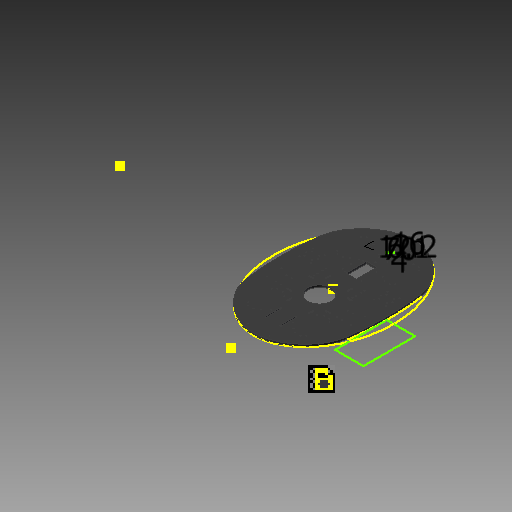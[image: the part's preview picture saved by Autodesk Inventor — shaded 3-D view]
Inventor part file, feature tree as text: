
AUTODESK INVENTOR PART (.ipt)
format: ipt  version: 2018 (Build 220112000, 112)  size: 756,224 bytes
history: native  units: in
note: dims shown in document units (in); Inventor stores cm internally (conversion verified against a paired STEP export)
features: reference x39, other x20, sketch x14, extrude x13, fillet x1, projected_geometry x1
ambient origin geometry x8: Origin, YZ Plane, XZ Plane, XY Plane, X Axis, Y Axis, Z Axis, Center Point
bodies: Body1 (feature_tree)
feature tree (88):
  extrude  "Extrusion2"  Depth=0.25in
  sketch  "Sketch2"  dims[d4=0.25in d5=0.0in d6=0.1969in]
  sketch  "Sketch3"  dims[d7=0.1969in d24=0.5in]
  extrude  "Extrusion13"  Depth=0.5in
  extrude  "Extrusion17"  Depth=0.0787in
  sketch  "Sketch12"  dims[d58=0.0787in d59=0.1575in d60=0.0787in d61=0.1575in]
  extrude  "Extrusion19"  Depth=0.0787in
  sketch  "Sketch14"  dims[d66=0.0787in d67=0.1575in d68=0.0787in d69=0.1575in d70=0.0787in d71=0.1575in]
  extrude  "Extrusion21"  Depth=0.0787in
  extrude  "Extrusion22"  Depth=0.0787in
  fillet  "Fillet1"  Radius=0.0787in
  sketch  "Sketch17"  dims[d76=0.0787in d77=0.1575in d78=0.0787in d79=0.1575in]
  extrude  "Extrusion24"  Depth=0.0787in
  extrude  "Extrusion25"  Depth=0.0787in
  extrude  "Extrusion26"  Depth=0.0787in
  extrude  "Extrusion27"  Depth=0.0787in TaperAngle=0.0deg
  extrude  "Extrusion28"  Depth=2.9528in
  extrude  "Extrusion29"  Depth=0.1437in
  extrude  "Extrusion30"  Depth=9.36in
  reference  "Reference1"
  reference  "Reference2"
  reference  "Reference3"
  reference  "Reference4"
  sketch  "Sketch9"  dims[d25=1.0in d48=0.0787in d49=0.1575in]
  reference  "Reference12"
  reference  "Reference13"
  reference  "Reference14"
  reference  "Reference15"
  reference  "Reference16"
  reference  "Reference17"
  reference  "Reference18"
  reference  "Reference19"
  reference  "Reference20"
  reference  "Reference21"
  reference  "Reference22"
  reference  "Reference23"
  reference  "Reference24"
  reference  "Reference25"
  reference  "Reference26"
  reference  "Reference27"
  reference  "Reference31"
  reference  "Reference32"
  reference  "Reference33"
  reference  "Reference34"
  reference  "Reference35"
  reference  "Reference36"
  reference  "Reference37"
  sketch  "Sketch13"  dims[d62=0.0787in d63=0.1575in d64=0.0787in d65=0.1575in]
  reference  "Reference38"
  reference  "Reference39"
  reference  "Reference40"
  reference  "Reference41"
  sketch  "Sketch16"  dims[d73=0.1575in d74=0.0787in d75=0.1575in]
  sketch  "Sketch18"  dims[d80=0.0787in d81=0.1575in d82=0.0787in d83=0.1575in]
  reference  "Reference46"
  reference  "Reference47"
  reference  "Reference48"
  reference  "Reference49"
  reference  "Reference50"
  reference  "Reference51"
  reference  "Reference52"
  reference  "Reference53"
  sketch  "Sketch19"  dims[d84=0.0787in d85=0.1575in d86=0.0787in d87=0.1575in d88=0.3937in d89=0.0in]
  sketch  "Sketch20"  dims[d90=3.0038in d91=2.9528in]
  sketch  "Sketch21"  dims[d92=0.1437in d93=0.1437in]
  projected_geometry  "Projected Loop1"
  sketch  "Sketch22"  dims[d103=9.36in d104=18.72in]
  sketch  "Sketch24"  dims[d105=7.0in d106=14.0in d107=3.0in d108=0.3937in d109=0.0in d110=0.1in d111=1.2in d112=2.7559in d113=0.1575in d116=0.3937in d117=0.0in d118=0.6299in d119=0.2402in d120=0.4803in d123=0.3937in d124=0.0in d125=3.937in d126=0.3937in d127=0.0in d128=5.0in d133=0.3937in d134=0.0in d141=1.2176in d142=2.7559in d143=0.5906in d145=0.3937in d146=0.0in d147=1.7717in d148=0.8858in d149=2.5504in d150=1.2752in d151=0.1181in d152=0.1181in d153=0.1181in d154=0.1181in d155=0.1181in d156=0.1181in d157=0.1181in d158=0.1181in d159=0.1181in d160=0.1181in d161=0.1283in d162=0.3937in d163=0.0in d164=0.1378in d165=0.1378in d166=0.3937in d167=0.0in d168=0.1378in d169=0.1378in d170=0.1378in d171=0.1378in d172=0.1378in d173=0.1378in d174=0.1378in d175=0.1378in d176=0.3937in d177=0.0in d178=0.1378in d179=0.1378in d180=0.1378in d181=0.1378in d182=0.3937in d183=0.0in d184=0.1378in d185=0.1378in d186=0.1378in d187=0.1378in d188=0.1378in d189=0.1378in d190=0.1378in d191=0.3937in d192=0.0in]
  other  "<userpath>\OneDrive\Documents\Inventor\TSA\2018\Animatronics\Tortoise\AssemblyTURTLE.iam"
  other  "AssemblyTURTLE.iam"
  other  "wheelframe:1"
  other  "wheelframe2:1"
  other  "correct_wheel:1"
  other  "steer_servo_mount:1"
  other  "holder_gear_mount:1"
  other  "holder_gear_mount:2"
  other  "holder_gear_mount:3"
  other  "<userpath>\OneDrive\Documents\Inventor\TSA\2018\Animatronics\Tortoise\TurtleAssembly.iam"
  other  "TurtleAssembly.iam"
  other  "BackWheelMount:1"
  other  "BackWheelServoClasp:1"
  other  "TailAssembly:1"
  other  "Tail_Servo_Mount:1"
  other  "Tail_Mount:1"
  other  "Rack:5"
  other  "GuideArmConnector:1"
  other  "GuideArmConnector:3"
  other  "Supporter:1"
